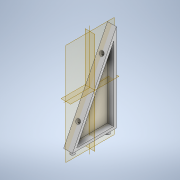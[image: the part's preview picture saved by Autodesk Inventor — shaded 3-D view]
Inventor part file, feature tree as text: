
AUTODESK INVENTOR PART (.ipt)
format: ipt  version: 2022.4 (Build 264492010, 492A)  size: 140,288 bytes
history: native  units: mm
features: extrude x4, sketch x4
ambient origin geometry x8: Origin, YZ Plane, XZ Plane, XY Plane, X Axis, Y Axis, Z Axis, Center Point
bodies: Solid1 (feature_tree)
feature tree (8):
  extrude  "Extrusion1"  Depth=100.0mm
  extrude  "Extrusion2"  Depth=3.0mm
  extrude  "Extrusion3"  Depth=5.0mm
  extrude  "Extrusion4"  Depth=10.0mm
  sketch  "Sketch2"  dims[d0=50.0mm d1=100.0mm]
  sketch  "Sketch4"  dims[d2=10.0mm d3=0.0mm d8=3.0mm]
  sketch  "Sketch5"  dims[d9=7.0mm d10=0.0mm d11=5.0mm]
  sketch  "Sketch8"  dims[d12=5.0mm d13=20.0mm d15=40.0mm d16=10.0mm d18=10.0mm d20=5.0mm d21=0.0mm d31=111.803399mm d32=5.0mm d34=30.0mm d35=7.0mm d36=0.0mm]
